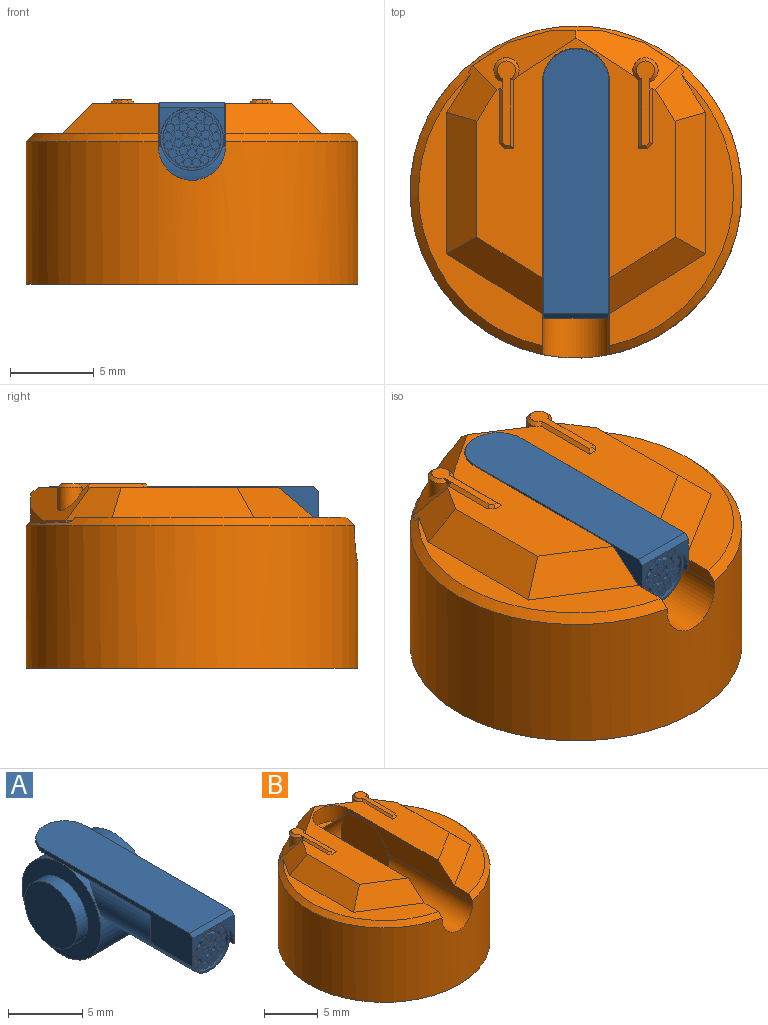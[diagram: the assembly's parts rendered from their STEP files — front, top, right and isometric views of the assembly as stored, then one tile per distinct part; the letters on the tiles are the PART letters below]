
ASSEMBLY  parts=2 mates=1
PART A: 296 faces, bbox 6x16.2x7.8 mm
  f0: cylinder r=1.88mm len=11.49mm, axis (0,1,0), area 101.5mm2, adj f2,f268,f270,f288,f289,f290,f291,f292
  f1: plane 3.47x3.47mm, normal (0,-1,0), area 3.4mm2, adj f3,f4,f5,f6,f7,f8,f9,f10
  f2: plane 3.75x3.75mm, normal (0,-1,0), area 1.6mm2, adj f0,f3,f272,f290,f291
  f3: cylinder r=1.73mm len=3.47mm, axis (0,1,0), area 3.7mm2, adj f1,f2
  f4: plane 0.2x0.18mm, normal (0.78,0,0.62), area 0mm2, adj f1,f5,f10,f11
  f5: plane 0.23x0.2mm, normal (0,0,1), area 0mm2, adj f1,f4,f6,f11
  f6: plane 0.2x0.18mm, normal (-0.78,0,0.62), area 0mm2, adj f1,f5,f7,f11
  f7: plane 0.23x0.2mm, normal (-0.97,0,-0.22), area 0mm2, adj f1,f6,f8,f11
  f8: plane 0.21x0.2mm, normal (-0.43,0,-0.9), area 0mm2, adj f1,f7,f9,f11
  f9: plane 0.21x0.2mm, normal (0.43,0,-0.9), area 0mm2, adj f1,f8,f10,f11
  f10: plane 0.23x0.2mm, normal (0.97,0,-0.22), area 0mm2, adj f1,f4,f9,f11
  f11: plane 0.52x0.51mm, normal (0,-1,0), area 0.2mm2, adj f4,f5,f6,f7,f8,f9,f10
  f12: plane 0.22x0.2mm, normal (-0.95,0,0.3), area 0mm2, adj f1,f13,f18,f19
  f13: plane 0.2x0.19mm, normal (-0.83,0,-0.56), area 0mm2, adj f1,f12,f14,f19
  f14: plane 0.23x0.2mm, normal (-0.08,0,-1), area 0mm2, adj f1,f13,f15,f19
  f15: plane 0.2x0.17mm, normal (0.73,0,-0.68), area 0mm2, adj f1,f14,f16,f19
  f16: plane 0.23x0.2mm, normal (0.99,0,0.14), area 0mm2, adj f1,f15,f17,f19
  f17: plane 0.2x0.2mm, normal (0.5,0,0.86), area 0mm2, adj f1,f16,f18,f19
  f18: plane 0.22x0.2mm, normal (-0.36,0,0.93), area 0mm2, adj f1,f12,f17,f19
  f19: plane 0.52x0.52mm, normal (0,-1,0), area 0.2mm2, adj f12,f13,f14,f15,f16,f17,f18
  f20: plane 0.23x0.2mm, normal (-1,0,-0.07), area 0mm2, adj f1,f21,f26,f27
  f21: plane 0.2x0.19mm, normal (-0.57,0,-0.82), area 0mm2, adj f1,f20,f22,f27
  f22: plane 0.22x0.2mm, normal (0.29,0,-0.96), area 0mm2, adj f1,f21,f23,f27
  f23: plane 0.22x0.2mm, normal (0.93,0,-0.37), area 0mm2, adj f1,f22,f24,f27
  f24: plane 0.2x0.2mm, normal (0.87,0,0.49), area 0mm2, adj f1,f23,f25,f27
  f25: plane 0.23x0.2mm, normal (0.16,0,0.99), area 0mm2, adj f1,f24,f26,f27
  f26: plane 0.2x0.17mm, normal (-0.67,0,0.74), area 0mm2, adj f1,f20,f25,f27
  f27: plane 0.52x0.52mm, normal (0,-1,0), area 0.2mm2, adj f20,f21,f22,f23,f24,f25,f26
  f28: plane 0.21x0.2mm, normal (-0.91,0,-0.42), area 0mm2, adj f1,f29,f34,f35
  f29: plane 0.23x0.2mm, normal (-0.24,0,-0.97), area 0mm2, adj f1,f28,f30,f35
  f30: plane 0.2x0.18mm, normal (0.61,0,-0.79), area 0mm2, adj f1,f29,f31,f35
  f31: plane 0.23x0.2mm, normal (1,0,-0.01), area 0mm2, adj f1,f30,f32,f35
  f32: plane 0.2x0.18mm, normal (0.63,0,0.77), area 0mm2, adj f1,f31,f33,f35
  f33: plane 0.23x0.2mm, normal (-0.21,0,0.98), area 0mm2, adj f1,f32,f34,f35
  f34: plane 0.21x0.2mm, normal (-0.9,0,0.45), area 0mm2, adj f1,f28,f33,f35
  f35: plane 0.52x0.51mm, normal (0,-1,0), area 0.2mm2, adj f28,f29,f30,f31,f32,f33,f34
  f36: plane 0.2x0.17mm, normal (-0.69,0,-0.72), area 0mm2, adj f1,f37,f42,f43
  f37: plane 0.23x0.2mm, normal (0.13,0,-0.99), area 0mm2, adj f1,f36,f38,f43
  f38: plane 0.2x0.2mm, normal (0.86,0,-0.52), area 0mm2, adj f1,f37,f39,f43
  f39: plane 0.22x0.2mm, normal (0.94,0,0.35), area 0mm2, adj f1,f38,f40,f43
  f40: plane 0.22x0.2mm, normal (0.31,0,0.95), area 0mm2, adj f1,f39,f41,f43
  f41: plane 0.2x0.2mm, normal (-0.55,0,0.84), area 0mm2, adj f1,f40,f42,f43
  f42: plane 0.23x0.2mm, normal (-1,0,0.09), area 0mm2, adj f1,f36,f41,f43
  f43: plane 0.52x0.52mm, normal (0,-1,0), area 0.2mm2, adj f36,f37,f38,f39,f40,f41,f42
  f44: plane 0.22x0.2mm, normal (-0.39,0,-0.92), area 0mm2, adj f1,f45,f50,f51
  f45: plane 0.2x0.2mm, normal (0.48,0,-0.88), area 0mm2, adj f1,f44,f46,f51
  f46: plane 0.23x0.2mm, normal (0.99,0,-0.17), area 0mm2, adj f1,f45,f47,f51
  f47: plane 0.2x0.17mm, normal (0.75,0,0.66), area 0mm2, adj f1,f46,f48,f51
  f48: plane 0.23x0.2mm, normal (-0.05,0,1), area 0mm2, adj f1,f47,f49,f51
  f49: plane 0.2x0.19mm, normal (-0.81,0,0.58), area 0mm2, adj f1,f48,f50,f51
  f50: plane 0.22x0.2mm, normal (-0.96,0,-0.27), area 0mm2, adj f1,f44,f49,f51
  f51: plane 0.52x0.52mm, normal (0,-1,0), area 0.2mm2, adj f44,f45,f46,f47,f48,f49,f50
  f52: plane 0.23x0.2mm, normal (-0.03,0,-1), area 0mm2, adj f1,f53,f58,f59
  f53: plane 0.2x0.18mm, normal (0.77,0,-0.64), area 0mm2, adj f1,f52,f54,f59
  f54: plane 0.23x0.2mm, normal (0.98,0,0.2), area 0mm2, adj f1,f53,f55,f59
  f55: plane 0.21x0.2mm, normal (0.46,0,0.89), area 0mm2, adj f1,f54,f56,f59
  f56: plane 0.21x0.2mm, normal (-0.41,0,0.91), area 0mm2, adj f1,f55,f57,f59
  f57: plane 0.23x0.2mm, normal (-0.97,0,0.25), area 0mm2, adj f1,f56,f58,f59
  f58: plane 0.2x0.19mm, normal (-0.8,0,-0.6), area 0mm2, adj f1,f52,f57,f59
  f59: plane 0.52x0.51mm, normal (0,-1,0), area 0.2mm2, adj f52,f53,f54,f55,f56,f57,f58
  f60: plane 0.22x0.2mm, normal (0.34,0,-0.94), area 0mm2, adj f1,f61,f66,f67
  f61: plane 0.22x0.2mm, normal (0.95,0,-0.32), area 0mm2, adj f1,f60,f62,f67
  f62: plane 0.2x0.2mm, normal (0.84,0,0.54), area 0mm2, adj f1,f61,f63,f67
  f63: plane 0.23x0.2mm, normal (0.11,0,0.99), area 0mm2, adj f1,f62,f64,f67
  f64: plane 0.2x0.17mm, normal (-0.71,0,0.7), area 0mm2, adj f1,f63,f65,f67
  f65: plane 0.23x0.2mm, normal (-0.99,0,-0.12), area 0mm2, adj f1,f64,f66,f67
  f66: plane 0.2x0.2mm, normal (-0.53,0,-0.85), area 0mm2, adj f1,f60,f65,f67
  f67: plane 0.52x0.52mm, normal (0,-1,0), area 0.2mm2, adj f60,f61,f62,f63,f64,f65,f66
  f68: plane 0.2x0.18mm, normal (0.65,0,-0.76), area 0mm2, adj f1,f69,f74,f75
  f69: plane 0.23x0.2mm, normal (1,0,0.04), area 0mm2, adj f1,f68,f70,f75
  f70: plane 0.2x0.19mm, normal (0.59,0,0.81), area 0mm2, adj f1,f69,f71,f75
  f71: plane 0.23x0.2mm, normal (-0.26,0,0.97), area 0mm2, adj f1,f70,f72,f75
  f72: plane 0.21x0.2mm, normal (-0.92,0,0.4), area 0mm2, adj f1,f71,f73,f75
  f73: plane 0.21x0.2mm, normal (-0.88,0,-0.47), area 0mm2, adj f1,f72,f74,f75
  f74: plane 0.23x0.2mm, normal (-0.18,0,-0.98), area 0mm2, adj f1,f68,f73,f75
  f75: plane 0.52x0.51mm, normal (0,-1,0), area 0.2mm2, adj f68,f69,f70,f71,f72,f73,f74
  f76: plane 0.21x0.2mm, normal (0.88,0,-0.47), area 0mm2, adj f1,f77,f82,f83
  f77: plane 0.21x0.2mm, normal (0.92,0,0.4), area 0mm2, adj f1,f76,f78,f83
  f78: plane 0.23x0.2mm, normal (0.26,0,0.97), area 0mm2, adj f1,f77,f79,f83
  f79: plane 0.2x0.19mm, normal (-0.59,0,0.81), area 0mm2, adj f1,f78,f80,f83
  f80: plane 0.23x0.2mm, normal (-1,0,0.04), area 0mm2, adj f1,f79,f81,f83
  f81: plane 0.2x0.18mm, normal (-0.65,0,-0.76), area 0mm2, adj f1,f80,f82,f83
  f82: plane 0.23x0.2mm, normal (0.18,0,-0.98), area 0mm2, adj f1,f76,f81,f83
  f83: plane 0.52x0.51mm, normal (0,-1,0), area 0.2mm2, adj f76,f77,f78,f79,f80,f81,f82
  f84: plane 0.23x0.2mm, normal (0.99,0,-0.12), area 0mm2, adj f1,f85,f90,f91
  f85: plane 0.2x0.17mm, normal (0.71,0,0.7), area 0mm2, adj f1,f84,f86,f91
  f86: plane 0.23x0.2mm, normal (-0.11,0,0.99), area 0mm2, adj f1,f85,f87,f91
  f87: plane 0.2x0.2mm, normal (-0.84,0,0.54), area 0mm2, adj f1,f86,f88,f91
  f88: plane 0.22x0.2mm, normal (-0.95,0,-0.32), area 0mm2, adj f1,f87,f89,f91
  f89: plane 0.22x0.2mm, normal (-0.34,0,-0.94), area 0mm2, adj f1,f88,f90,f91
  f90: plane 0.2x0.2mm, normal (0.53,0,-0.85), area 0mm2, adj f1,f84,f89,f91
  f91: plane 0.52x0.52mm, normal (0,-1,0), area 0.2mm2, adj f84,f85,f86,f87,f88,f89,f90
  f92: plane 0.23x0.2mm, normal (0.97,0,0.25), area 0mm2, adj f1,f93,f98,f99
  f93: plane 0.21x0.2mm, normal (0.41,0,0.91), area 0mm2, adj f1,f92,f94,f99
  f94: plane 0.21x0.2mm, normal (-0.46,0,0.89), area 0mm2, adj f1,f93,f95,f99
  f95: plane 0.23x0.2mm, normal (-0.98,0,0.2), area 0mm2, adj f1,f94,f96,f99
  f96: plane 0.2x0.18mm, normal (-0.77,0,-0.64), area 0mm2, adj f1,f95,f97,f99
  f97: plane 0.23x0.2mm, normal (0.03,0,-1), area 0mm2, adj f1,f96,f98,f99
  f98: plane 0.2x0.19mm, normal (0.8,0,-0.6), area 0mm2, adj f1,f92,f97,f99
  f99: plane 0.52x0.51mm, normal (0,-1,0), area 0.2mm2, adj f92,f93,f94,f95,f96,f97,f98
  f100: plane 0.2x0.19mm, normal (0.81,0,0.58), area 0mm2, adj f1,f101,f106,f107
  f101: plane 0.23x0.2mm, normal (0.05,0,1), area 0mm2, adj f1,f100,f102,f107
  f102: plane 0.2x0.17mm, normal (-0.75,0,0.66), area 0mm2, adj f1,f101,f103,f107
  f103: plane 0.23x0.2mm, normal (-0.99,0,-0.17), area 0mm2, adj f1,f102,f104,f107
  f104: plane 0.2x0.2mm, normal (-0.48,0,-0.88), area 0mm2, adj f1,f103,f105,f107
  f105: plane 0.22x0.2mm, normal (0.39,0,-0.92), area 0mm2, adj f1,f104,f106,f107
  f106: plane 0.22x0.2mm, normal (0.96,0,-0.27), area 0mm2, adj f1,f100,f105,f107
  f107: plane 0.52x0.52mm, normal (0,-1,0), area 0.2mm2, adj f100,f101,f102,f103,f104,f105,f106
  f108: plane 0.2x0.2mm, normal (0.55,0,0.84), area 0mm2, adj f1,f109,f114,f115
  f109: plane 0.22x0.2mm, normal (-0.31,0,0.95), area 0mm2, adj f1,f108,f110,f115
  f110: plane 0.22x0.2mm, normal (-0.94,0,0.35), area 0mm2, adj f1,f109,f111,f115
  f111: plane 0.2x0.2mm, normal (-0.86,0,-0.52), area 0mm2, adj f1,f110,f112,f115
  f112: plane 0.23x0.2mm, normal (-0.13,0,-0.99), area 0mm2, adj f1,f111,f113,f115
  f113: plane 0.2x0.17mm, normal (0.69,0,-0.72), area 0mm2, adj f1,f112,f114,f115
  f114: plane 0.23x0.2mm, normal (1,0,0.09), area 0mm2, adj f1,f108,f113,f115
  f115: plane 0.52x0.52mm, normal (0,-1,0), area 0.2mm2, adj f108,f109,f110,f111,f112,f113,f114
  f116: plane 0.23x0.2mm, normal (0.21,0,0.98), area 0mm2, adj f1,f117,f122,f123
  f117: plane 0.2x0.18mm, normal (-0.63,0,0.77), area 0mm2, adj f1,f116,f118,f123
  f118: plane 0.23x0.2mm, normal (-1,0,-0.01), area 0mm2, adj f1,f117,f119,f123
  f119: plane 0.2x0.18mm, normal (-0.61,0,-0.79), area 0mm2, adj f1,f118,f120,f123
  f120: plane 0.23x0.2mm, normal (0.24,0,-0.97), area 0mm2, adj f1,f119,f121,f123
  f121: plane 0.21x0.2mm, normal (0.91,0,-0.42), area 0mm2, adj f1,f120,f122,f123
  f122: plane 0.21x0.2mm, normal (0.9,0,0.45), area 0mm2, adj f1,f116,f121,f123
  f123: plane 0.52x0.51mm, normal (0,-1,0), area 0.2mm2, adj f116,f117,f118,f119,f120,f121,f122
  f124: plane 0.23x0.2mm, normal (-0.16,0,0.99), area 0mm2, adj f1,f125,f130,f131
  f125: plane 0.2x0.2mm, normal (-0.87,0,0.49), area 0mm2, adj f1,f124,f126,f131
  f126: plane 0.22x0.2mm, normal (-0.93,0,-0.37), area 0mm2, adj f1,f125,f127,f131
  f127: plane 0.22x0.2mm, normal (-0.29,0,-0.96), area 0mm2, adj f1,f126,f128,f131
  f128: plane 0.2x0.19mm, normal (0.57,0,-0.82), area 0mm2, adj f1,f127,f129,f131
  f129: plane 0.23x0.2mm, normal (1,0,-0.07), area 0mm2, adj f1,f128,f130,f131
  f130: plane 0.2x0.17mm, normal (0.67,0,0.74), area 0mm2, adj f1,f124,f129,f131
  f131: plane 0.52x0.52mm, normal (0,-1,0), area 0.2mm2, adj f124,f125,f126,f127,f128,f129,f130
  f132: plane 0.2x0.2mm, normal (-0.5,0,0.86), area 0mm2, adj f1,f133,f138,f139
  f133: plane 0.23x0.2mm, normal (-0.99,0,0.14), area 0mm2, adj f1,f132,f134,f139
  f134: plane 0.2x0.17mm, normal (-0.73,0,-0.68), area 0mm2, adj f1,f133,f135,f139
  f135: plane 0.23x0.2mm, normal (0.08,0,-1), area 0mm2, adj f1,f134,f136,f139
  f136: plane 0.2x0.19mm, normal (0.83,0,-0.56), area 0mm2, adj f1,f135,f137,f139
  f137: plane 0.22x0.2mm, normal (0.95,0,0.3), area 0mm2, adj f1,f136,f138,f139
  f138: plane 0.22x0.2mm, normal (0.36,0,0.93), area 0mm2, adj f1,f132,f137,f139
  f139: plane 0.52x0.52mm, normal (0,-1,0), area 0.2mm2, adj f132,f133,f134,f135,f136,f137,f138
  f140: plane 0.2x0.18mm, normal (0.78,0,0.62), area 0mm2, adj f1,f141,f146,f147
  f141: plane 0.23x0.2mm, normal (0,0,1), area 0mm2, adj f1,f140,f142,f147
  f142: plane 0.2x0.18mm, normal (-0.78,0,0.62), area 0mm2, adj f1,f141,f143,f147
  f143: plane 0.23x0.2mm, normal (-0.97,0,-0.22), area 0mm2, adj f1,f142,f144,f147
  f144: plane 0.21x0.2mm, normal (-0.43,0,-0.9), area 0mm2, adj f1,f143,f145,f147
  f145: plane 0.21x0.2mm, normal (0.43,0,-0.9), area 0mm2, adj f1,f144,f146,f147
  f146: plane 0.23x0.2mm, normal (0.97,0,-0.22), area 0mm2, adj f1,f140,f145,f147
  f147: plane 0.52x0.51mm, normal (0,-1,0), area 0.2mm2, adj f140,f141,f142,f143,f144,f145,f146
  f148: plane 0.2x0.17mm, normal (0.68,0,-0.73), area 0mm2, adj f1,f149,f154,f155
  f149: plane 0.23x0.2mm, normal (1,0,0.07), area 0mm2, adj f1,f148,f150,f155
  f150: plane 0.2x0.19mm, normal (0.56,0,0.83), area 0mm2, adj f1,f149,f151,f155
  f151: plane 0.22x0.2mm, normal (-0.29,0,0.96), area 0mm2, adj f1,f150,f152,f155
  f152: plane 0.22x0.2mm, normal (-0.93,0,0.37), area 0mm2, adj f1,f151,f153,f155
  f153: plane 0.2x0.2mm, normal (-0.87,0,-0.5), area 0mm2, adj f1,f152,f154,f155
  f154: plane 0.23x0.2mm, normal (-0.15,0,-0.99), area 0mm2, adj f1,f148,f153,f155
  f155: plane 0.52x0.51mm, normal (0,-1,0), area 0.2mm2, adj f148,f149,f150,f151,f152,f153,f154
  f156: plane 0.22x0.2mm, normal (0.29,0,0.96), area 0mm2, adj f1,f157,f162,f163
  f157: plane 0.2x0.19mm, normal (-0.56,0,0.83), area 0mm2, adj f1,f156,f158,f163
  f158: plane 0.23x0.2mm, normal (-1,0,0.07), area 0mm2, adj f1,f157,f159,f163
  f159: plane 0.2x0.17mm, normal (-0.68,0,-0.73), area 0mm2, adj f1,f158,f160,f163
  f160: plane 0.23x0.2mm, normal (0.15,0,-0.99), area 0mm2, adj f1,f159,f161,f163
  f161: plane 0.2x0.2mm, normal (0.87,0,-0.5), area 0mm2, adj f1,f160,f162,f163
  f162: plane 0.22x0.2mm, normal (0.93,0,0.37), area 0mm2, adj f1,f156,f161,f163
  f163: plane 0.52x0.51mm, normal (0,-1,0), area 0.2mm2, adj f156,f157,f158,f159,f160,f161,f162
  f164: plane 0.3x0.18mm, normal (0.78,0,0.62), area 0.1mm2, adj f1,f165,f170,f171
  f165: plane 0.3x0.23mm, normal (0,0,1), area 0.1mm2, adj f1,f164,f166,f171
  f166: plane 0.3x0.18mm, normal (-0.78,0,0.62), area 0.1mm2, adj f1,f165,f167,f171
  f167: plane 0.3x0.23mm, normal (-0.97,0,-0.22), area 0.1mm2, adj f1,f166,f168,f171
  f168: plane 0.3x0.21mm, normal (-0.43,0,-0.9), area 0.1mm2, adj f1,f167,f169,f171
  f169: plane 0.3x0.21mm, normal (0.43,0,-0.9), area 0.1mm2, adj f1,f168,f170,f171
  f170: plane 0.3x0.23mm, normal (0.97,0,-0.22), area 0.1mm2, adj f1,f164,f169,f171
  f171: plane 0.52x0.51mm, normal (0,-1,0), area 0.2mm2, adj f164,f165,f166,f167,f168,f169,f170
  f172: plane 0.3x0.2mm, normal (0.88,0,-0.47), area 0.1mm2, adj f1,f173,f178,f179
  f173: plane 0.3x0.21mm, normal (0.92,0,0.39), area 0.1mm2, adj f1,f172,f174,f179
  f174: plane 0.3x0.22mm, normal (0.27,0,0.96), area 0.1mm2, adj f1,f173,f175,f179
  f175: plane 0.3x0.19mm, normal (-0.59,0,0.81), area 0.1mm2, adj f1,f174,f176,f179
  f176: plane 0.3x0.23mm, normal (-1,0,0.04), area 0.1mm2, adj f1,f175,f177,f179
  f177: plane 0.3x0.17mm, normal (-0.66,0,-0.75), area 0.1mm2, adj f1,f176,f178,f179
  f178: plane 0.3x0.23mm, normal (0.18,0,-0.98), area 0.1mm2, adj f1,f172,f177,f179
  f179: plane 0.52x0.51mm, normal (0,-1,0), area 0.2mm2, adj f172,f173,f174,f175,f176,f177,f178
  f180: plane 0.3x0.23mm, normal (0.99,0,0.13), area 0.1mm2, adj f1,f181,f186,f187
  f181: plane 0.3x0.2mm, normal (0.51,0,0.86), area 0.1mm2, adj f1,f180,f182,f187
  f182: plane 0.3x0.22mm, normal (-0.35,0,0.94), area 0.1mm2, adj f1,f181,f183,f187
  f183: plane 0.3x0.22mm, normal (-0.95,0,0.31), area 0.1mm2, adj f1,f182,f184,f187
  f184: plane 0.3x0.19mm, normal (-0.83,0,-0.55), area 0.1mm2, adj f1,f183,f185,f187
  f185: plane 0.3x0.23mm, normal (-0.09,0,-1), area 0.1mm2, adj f1,f184,f186,f187
  f186: plane 0.3x0.17mm, normal (0.72,0,-0.69), area 0.1mm2, adj f1,f180,f185,f187
  f187: plane 0.52x0.51mm, normal (0,-1,0), area 0.2mm2, adj f180,f181,f182,f183,f184,f185,f186
  f188: plane 0.3x0.17mm, normal (0.72,0,0.69), area 0.1mm2, adj f1,f189,f194,f195
  f189: plane 0.3x0.23mm, normal (-0.09,0,1), area 0.1mm2, adj f1,f188,f190,f195
  f190: plane 0.3x0.19mm, normal (-0.83,0,0.55), area 0.1mm2, adj f1,f189,f191,f195
  f191: plane 0.3x0.22mm, normal (-0.95,0,-0.31), area 0.1mm2, adj f1,f190,f192,f195
  f192: plane 0.3x0.22mm, normal (-0.35,0,-0.94), area 0.1mm2, adj f1,f191,f193,f195
  f193: plane 0.3x0.2mm, normal (0.51,0,-0.86), area 0.1mm2, adj f1,f192,f194,f195
  f194: plane 0.3x0.23mm, normal (0.99,0,-0.13), area 0.1mm2, adj f1,f188,f193,f195
  f195: plane 0.52x0.51mm, normal (0,-1,0), area 0.2mm2, adj f188,f189,f190,f191,f192,f193,f194
  f196: plane 0.3x0.23mm, normal (0.18,0,0.98), area 0.1mm2, adj f1,f197,f202,f203
  f197: plane 0.3x0.17mm, normal (-0.66,0,0.75), area 0.1mm2, adj f1,f196,f198,f203
  f198: plane 0.3x0.23mm, normal (-1,0,-0.04), area 0.1mm2, adj f1,f197,f199,f203
  f199: plane 0.3x0.19mm, normal (-0.59,0,-0.81), area 0.1mm2, adj f1,f198,f200,f203
  f200: plane 0.3x0.22mm, normal (0.27,0,-0.96), area 0.1mm2, adj f1,f199,f201,f203
  f201: plane 0.3x0.21mm, normal (0.92,0,-0.39), area 0.1mm2, adj f1,f200,f202,f203
  f202: plane 0.3x0.2mm, normal (0.88,0,0.47), area 0.1mm2, adj f1,f196,f201,f203
  f203: plane 0.52x0.51mm, normal (0,-1,0), area 0.2mm2, adj f196,f197,f198,f199,f200,f201,f202
  f204: plane 0.3x0.21mm, normal (-0.43,0,0.9), area 0.1mm2, adj f1,f205,f210,f211
  f205: plane 0.3x0.23mm, normal (-0.97,0,0.22), area 0.1mm2, adj f1,f204,f206,f211
  f206: plane 0.3x0.18mm, normal (-0.78,0,-0.62), area 0.1mm2, adj f1,f205,f207,f211
  f207: plane 0.3x0.23mm, normal (0,0,-1), area 0.1mm2, adj f1,f206,f208,f211
  f208: plane 0.3x0.18mm, normal (0.78,0,-0.62), area 0.1mm2, adj f1,f207,f209,f211
  f209: plane 0.3x0.23mm, normal (0.97,0,0.22), area 0.1mm2, adj f1,f208,f210,f211
  f210: plane 0.3x0.21mm, normal (0.43,0,0.9), area 0.1mm2, adj f1,f204,f209,f211
  f211: plane 0.52x0.51mm, normal (0,-1,0), area 0.2mm2, adj f204,f205,f206,f207,f208,f209,f210
  f212: plane 0.3x0.2mm, normal (-0.88,0,0.47), area 0.1mm2, adj f1,f213,f218,f219
  f213: plane 0.3x0.21mm, normal (-0.92,0,-0.39), area 0.1mm2, adj f1,f212,f214,f219
  f214: plane 0.3x0.22mm, normal (-0.27,0,-0.96), area 0.1mm2, adj f1,f213,f215,f219
  f215: plane 0.3x0.19mm, normal (0.59,0,-0.81), area 0.1mm2, adj f1,f214,f216,f219
  f216: plane 0.3x0.23mm, normal (1,0,-0.04), area 0.1mm2, adj f1,f215,f217,f219
  f217: plane 0.3x0.17mm, normal (0.66,0,0.75), area 0.1mm2, adj f1,f216,f218,f219
  f218: plane 0.3x0.23mm, normal (-0.18,0,0.98), area 0.1mm2, adj f1,f212,f217,f219
  f219: plane 0.52x0.51mm, normal (0,-1,0), area 0.2mm2, adj f212,f213,f214,f215,f216,f217,f218
  f220: plane 0.3x0.23mm, normal (-0.99,0,-0.13), area 0.1mm2, adj f1,f221,f226,f227
  f221: plane 0.3x0.2mm, normal (-0.51,0,-0.86), area 0.1mm2, adj f1,f220,f222,f227
  f222: plane 0.3x0.22mm, normal (0.35,0,-0.94), area 0.1mm2, adj f1,f221,f223,f227
  f223: plane 0.3x0.22mm, normal (0.95,0,-0.31), area 0.1mm2, adj f1,f222,f224,f227
  f224: plane 0.3x0.19mm, normal (0.83,0,0.55), area 0.1mm2, adj f1,f223,f225,f227
  f225: plane 0.3x0.23mm, normal (0.09,0,1), area 0.1mm2, adj f1,f224,f226,f227
  f226: plane 0.3x0.17mm, normal (-0.72,0,0.69), area 0.1mm2, adj f1,f220,f225,f227
  f227: plane 0.52x0.51mm, normal (0,-1,0), area 0.2mm2, adj f220,f221,f222,f223,f224,f225,f226
  f228: plane 0.3x0.17mm, normal (-0.72,0,-0.69), area 0.1mm2, adj f1,f229,f234,f235
  f229: plane 0.3x0.23mm, normal (0.09,0,-1), area 0.1mm2, adj f1,f228,f230,f235
  f230: plane 0.3x0.19mm, normal (0.83,0,-0.55), area 0.1mm2, adj f1,f229,f231,f235
  f231: plane 0.3x0.22mm, normal (0.95,0,0.31), area 0.1mm2, adj f1,f230,f232,f235
  f232: plane 0.3x0.22mm, normal (0.35,0,0.94), area 0.1mm2, adj f1,f231,f233,f235
  f233: plane 0.3x0.2mm, normal (-0.51,0,0.86), area 0.1mm2, adj f1,f232,f234,f235
  f234: plane 0.3x0.23mm, normal (-0.99,0,0.13), area 0.1mm2, adj f1,f228,f233,f235
  f235: plane 0.52x0.51mm, normal (0,-1,0), area 0.2mm2, adj f228,f229,f230,f231,f232,f233,f234
  f236: plane 0.3x0.23mm, normal (-0.18,0,-0.98), area 0.1mm2, adj f1,f237,f242,f243
  f237: plane 0.3x0.17mm, normal (0.66,0,-0.75), area 0.1mm2, adj f1,f236,f238,f243
  f238: plane 0.3x0.23mm, normal (1,0,0.04), area 0.1mm2, adj f1,f237,f239,f243
  f239: plane 0.3x0.19mm, normal (0.59,0,0.81), area 0.1mm2, adj f1,f238,f240,f243
  f240: plane 0.3x0.22mm, normal (-0.27,0,0.96), area 0.1mm2, adj f1,f239,f241,f243
  f241: plane 0.3x0.21mm, normal (-0.92,0,0.39), area 0.1mm2, adj f1,f240,f242,f243
  f242: plane 0.3x0.2mm, normal (-0.88,0,-0.47), area 0.1mm2, adj f1,f236,f241,f243
  f243: plane 0.52x0.51mm, normal (0,-1,0), area 0.2mm2, adj f236,f237,f238,f239,f240,f241,f242
  f244: plane 0.1x0.08mm, normal (0.78,0,0.62), area 0mm2, adj f1,f245,f250,f251
  f245: plane 0.11x0.1mm, normal (0,0,1), area 0mm2, adj f1,f244,f246,f251
  f246: plane 0.1x0.08mm, normal (-0.78,0,0.62), area 0mm2, adj f1,f245,f247,f251
  f247: plane 0.1x0.1mm, normal (-0.97,0,-0.22), area 0mm2, adj f1,f246,f248,f251
  f248: plane 0.1x0.1mm, normal (-0.43,0,-0.9), area 0mm2, adj f1,f247,f249,f251
  f249: plane 0.1x0.1mm, normal (0.43,0,-0.9), area 0mm2, adj f1,f248,f250,f251
  f250: plane 0.1x0.1mm, normal (0.97,0,-0.22), area 0mm2, adj f1,f244,f249,f251
  f251: plane 0.24x0.23mm, normal (0,-1,0), area 0mm2, adj f244,f245,f246,f247,f248,f249,f250
  f252: plane 0.1x0.09mm, normal (-0.87,0,-0.5), area 0mm2, adj f1,f253,f258,f259
  f253: plane 0.11x0.1mm, normal (-0.15,0,-0.99), area 0mm2, adj f1,f252,f254,f259
  f254: plane 0.1x0.08mm, normal (0.68,0,-0.73), area 0mm2, adj f1,f253,f255,f259
  f255: plane 0.11x0.1mm, normal (1,0,0.07), area 0mm2, adj f1,f254,f256,f259
  f256: plane 0.1x0.09mm, normal (0.56,0,0.83), area 0mm2, adj f1,f255,f257,f259
  f257: plane 0.1x0.1mm, normal (-0.29,0,0.96), area 0mm2, adj f1,f256,f258,f259
  f258: plane 0.1x0.1mm, normal (-0.93,0,0.37), area 0mm2, adj f1,f252,f257,f259
  f259: plane 0.24x0.24mm, normal (0,-1,0), area 0mm2, adj f252,f253,f254,f255,f256,f257,f258
  f260: plane 0.1x0.09mm, normal (0.87,0,-0.5), area 0mm2, adj f1,f261,f266,f267
  f261: plane 0.1x0.1mm, normal (0.93,0,0.37), area 0mm2, adj f1,f260,f262,f267
  f262: plane 0.1x0.1mm, normal (0.29,0,0.96), area 0mm2, adj f1,f261,f263,f267
  f263: plane 0.1x0.09mm, normal (-0.56,0,0.83), area 0mm2, adj f1,f262,f264,f267
  f264: plane 0.11x0.1mm, normal (-1,0,0.07), area 0mm2, adj f1,f263,f265,f267
  f265: plane 0.1x0.08mm, normal (-0.68,0,-0.73), area 0mm2, adj f1,f264,f266,f267
  f266: plane 0.11x0.1mm, normal (0.15,0,-0.99), area 0mm2, adj f1,f260,f265,f267
  f267: plane 0.24x0.24mm, normal (0,-1,0), area 0mm2, adj f260,f261,f262,f263,f264,f265,f266
  f268: cylinder r=3.75mm len=7.5mm, axis (-1,0,0), area 98.3mm2, adj f0,f269,f270,f271,f275,f277,f292,f294
  f269: plane 7.5x7.5mm, normal (1,0,0), area 44.2mm2, adj f268
  f270: plane 7.82x1.53mm, normal (0,0,-1), area 11.9mm2, adj f0,f268,f275,f286,f289
  f271: plane 3.91x3.02mm, normal (0,0,-1), area 10.2mm2, adj f268,f275,f276,f277
  f272: plane 0.48x0.33mm, normal (0,0,-1), area 0.2mm2, adj f2,f279,f285,f287
  f273: plane 2.32x1.72mm, normal (0,-1,0), area 0.9mm2, adj f275,f283,f284,f285,f287
  f274: plane 2.32x1.72mm, normal (0,-1,0), area 0.9mm2, adj f277,f279,f280,f281,f287
  f275: plane 14.11x2.62mm, normal (1,0,0), area 13.9mm2, adj f268,f270,f271,f273,f276,f278,f284,f286
  f276: cylinder r=1.96mm len=3.91mm, axis (0,0,-1), area 2.1mm2, adj f271,f275,f277,f278
  f277: plane 14.11x2.62mm, normal (-1,0,0), area 13.9mm2, adj f268,f271,f274,f276,f278,f280,f282,f287
  f278: plane 15.76x3.91mm, normal (0,0,1), area 60mm2, adj f275,f276,f277,f287
  f279: cylinder r=1.89mm len=4mm, axis (0,-1,0), area 10.9mm2, adj f272,f274,f281,f282,f288,f291
  f280: plane 4x0.07mm, normal (0,0,-1), area 0.3mm2, adj f274,f277,f281,f282
  f281: plane 4x0.45mm, normal (1,0,0), area 1.8mm2, adj f274,f279,f280,f282
  f282: plane 2.27x1.46mm, normal (0,1,0), area 0.8mm2, adj f277,f279,f280,f281,f292
  f283: plane 4x0.45mm, normal (-1,0,0), area 1.8mm2, adj f273,f284,f285,f286
  f284: plane 4x0.07mm, normal (0,0,-1), area 0.3mm2, adj f273,f275,f283,f286
  f285: cylinder r=1.89mm len=4mm, axis (0,-1,0), area 10.9mm2, adj f272,f273,f283,f286,f289,f290
  f286: plane 2.27x1.46mm, normal (0,1,0), area 0.8mm2, adj f270,f275,f283,f284,f285
  f287: plane 3.91x0.3mm, normal (0,-0.71,0.71), area 1.7mm2, adj f272,f273,f274,f275,f277,f278
  f288: plane 0.25x0.05mm, normal (0,-1,0), area 0mm2, adj f0,f279,f291,f292
  f289: plane 0.25x0.05mm, normal (0,-1,0), area 0mm2, adj f0,f270,f285,f290
  f290: plane 3.67x0.02mm, normal (1,0,0), area 0.1mm2, adj f0,f2,f285,f289
  f291: plane 3.67x0.02mm, normal (-1,0,0), area 0.1mm2, adj f0,f2,f279,f288
  f292: plane 7.82x1.53mm, normal (0,0,-1), area 11.9mm2, adj f0,f268,f277,f282,f288
  f293: cylinder r=2.5mm len=5mm, axis (1,0,0), area 15.7mm2, adj f294,f295
  f294: plane 7.5x7.5mm, normal (-1,0,0), area 24.5mm2, adj f268,f293
  f295: plane 5x5mm, normal (-1,0,0), area 19.6mm2, adj f293
PART B: 46 faces, bbox 20.1x20.1x11.3 mm
  f0: cylinder r=2mm len=4mm, axis (0,0,-1), area 9.6mm2, adj f1,f10,f11,f18,f44
  f1: plane 2.93x0.64mm, normal (0,0,1), area 1.3mm2, adj f0,f44
  f2: cylinder r=2mm len=11.12mm, axis (0,1,0), area 69.9mm2, adj f10,f18,f40,f44
  f3: cylinder r=2.5mm len=5mm, axis (1,0,0), area 15.7mm2, adj f18,f43
  f4: plane 6.18x3.56mm, normal (-0.39,0.59,0.71), area 11.2mm2, adj f5,f9,f11,f16,f17,f21,f26,f27
  f5: plane 6.18x3.56mm, normal (0.39,0.59,0.71), area 11.2mm2, adj f4,f7,f8,f9,f11,f14,f22,f23
  f6: plane 0.42x0.27mm, normal (0.84,0.54,0), area 0mm2, adj f7,f14,f41
  f7: plane 2.34x1.6mm, normal (0.55,0.84,0), area 0.3mm2, adj f5,f6,f8,f41
  f8: plane 2.8x1.21mm, normal (0.28,0.96,0), area 1.3mm2, adj f5,f7,f9,f41
  f9: plane 3.06x1.76mm, normal (0,1,0), area 3.9mm2, adj f4,f5,f8,f17,f41
  f10: plane 16.27x2.6mm, normal (-1,0,0), area 26.3mm2, adj f0,f2,f11,f12,f38,f40,f41,f44
  f11: plane 14.31x11.85mm, normal (0,0,1), area 76.1mm2, adj f0,f4,f5,f10,f12,f13,f14,f18
  f12: plane 5.72x4.58mm, normal (0.38,-0.6,0.71), area 14.5mm2, adj f10,f11,f13,f38
  f13: plane 8.45x1.8mm, normal (0.71,0,0.71), area 19.6mm2, adj f11,f12,f14,f38
  f14: plane 3.3x2.99mm, normal (0.59,0.38,0.71), area 6.9mm2, adj f5,f6,f11,f13,f38,f41
  f15: plane 0.42x0.27mm, normal (-0.84,0.54,0), area 0mm2, adj f16,f21,f41
  f16: plane 2.34x1.6mm, normal (-0.55,0.84,0), area 0.3mm2, adj f4,f15,f17,f41
  f17: plane 2.8x1.21mm, normal (-0.28,0.96,0), area 1.3mm2, adj f4,f9,f16,f41
  f18: plane 18.35x7.75mm, normal (1,0,0), area 50.8mm2, adj f0,f2,f3,f11,f19,f39,f40,f41
  f19: plane 5.72x4.58mm, normal (-0.38,-0.6,0.71), area 14.5mm2, adj f11,f18,f20,f39
  f20: plane 8.45x1.8mm, normal (-0.71,0,0.71), area 19.6mm2, adj f11,f19,f21,f39
  f21: plane 3.3x2.99mm, normal (-0.59,0.38,0.71), area 6.9mm2, adj f4,f11,f15,f20,f39,f41
  f22: cylinder r=0.75mm len=1.5mm, axis (0,0,-1), area 3.2mm2, adj f5,f23,f25
  f23: plane 0.69x0.4mm, normal (1,0,0), area 0.1mm2, adj f5,f22,f24,f25
  f24: plane 5.05x1.1mm, normal (0,0,1), area 2.7mm2, adj f23,f25,f34,f35,f36,f37
  f25: cone r=0.55mm half-angle=45deg, axis (0,0,-1), area 1mm2, adj f11,f22,f23,f24,f37
  f26: cylinder r=0.75mm len=1.5mm, axis (0,0,-1), area 3.2mm2, adj f4,f27,f29
  f27: plane 0.69x0.4mm, normal (-1,0,0), area 0.1mm2, adj f4,f26,f28,f29
  f28: plane 5.05x1.1mm, normal (0,0,1), area 2.7mm2, adj f27,f29,f30,f31,f32,f33
  f29: cone r=0.55mm half-angle=45deg, axis (0,0,-1), area 1mm2, adj f11,f26,f27,f28,f30
  f30: plane 4.21x0.21mm, normal (0.71,0,0.71), area 1.1mm2, adj f11,f28,f29,f31
  f31: plane 0.53x0.2mm, normal (0,-0.71,0.71), area 0.1mm2, adj f11,f28,f30,f32
  f32: plane 0.4x0.4mm, normal (-0.5,-0.5,0.71), area 0.1mm2, adj f11,f28,f31,f33
  f33: plane 3.3x0.2mm, normal (-0.71,0,0.71), area 0.9mm2, adj f4,f11,f28,f32
  f34: plane 3.3x0.2mm, normal (0.71,0,0.71), area 0.9mm2, adj f5,f11,f24,f35
  f35: plane 0.4x0.4mm, normal (0.5,-0.5,0.71), area 0.1mm2, adj f11,f24,f34,f36
  f36: plane 0.53x0.2mm, normal (0,-0.71,0.71), area 0.1mm2, adj f11,f24,f35,f37
  f37: plane 4.21x0.21mm, normal (-0.71,0,0.71), area 1.1mm2, adj f11,f24,f25,f36
  f38: plane 16.17x7.4mm, normal (0,0,1), area 26mm2, adj f10,f12,f13,f14,f41
  f39: plane 16.17x7.4mm, normal (0,0,1), area 26mm2, adj f18,f19,f20,f21,f41
  f40: cylinder r=9.9mm len=19.8mm, axis (0,0,-1), area 521.2mm2, adj f2,f10,f18,f41,f42
  f41: cone r=9.4mm half-angle=45deg, axis (0,0,-1), area 33.3mm2, adj f6,f7,f8,f9,f10,f14,f15,f16
  f42: plane 19.8x19.8mm, normal (0,0,-1), area 307.9mm2, adj f40
  f43: plane 5x5mm, normal (1,0,0), area 19.6mm2, adj f3
  f44: cylinder r=3.75mm len=7.5mm, axis (-1,0,0), area 80.4mm2, adj f0,f1,f2,f10,f18,f45
  f45: plane 7.5x7.5mm, normal (-1,0,0), area 44.2mm2, adj f44
PLACE A t=(-0.22,-1.22,-3.54)mm
PLACE B t=(-0.22,-1.22,-3.54)mm
MATE revolute A.f268 <-> B.f3  axis (-1,0,0) through (-3.22,3.68,3.26)mm
